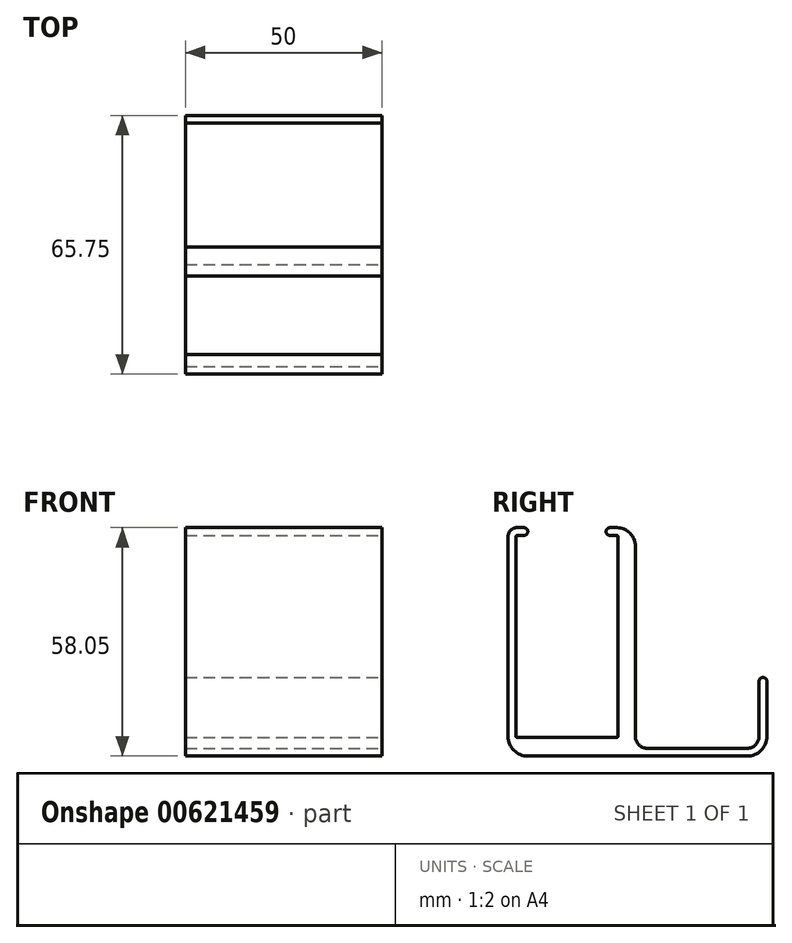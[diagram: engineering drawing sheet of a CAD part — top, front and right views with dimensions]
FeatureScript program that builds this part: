
annotation { "Feature Type Name" : "Feature", "Feature Type Description" : "" }
export const myFeature = defineFeature(function(context is Context, id is Id, definition is map)
    precondition{}
    {
        {
            var Q0;
            Q0=qCreatedBy(makeId("Right.planeOp"),FACE);
            var sketch = newSketch(context, id + "F0", { "sketchPlane" : qUnion([Q0])});
            skLineSegment(sketch, "E0.bottom", {"start": v(-33.1, 50.8) * mm, "end": v(-7.7, 50.8) * mm});
            skLineSegment(sketch, "E0.top", {"start": v(-33.1, 0) * mm, "end": v(-7.7, 0) * mm});
            skLineSegment(sketch, "E0.left", {"start": v(-33.1, 50.8) * mm, "end": v(-33.1, 0) * mm});
            skLineSegment(sketch, "E0.right", {"start": v(-7.7, 50.8) * mm, "end": v(-7.7, 0) * mm});
            skLineSegment(sketch, "E1.bottom", {"start": v(0, 0) * mm, "end": v(25.4, 0) * mm});
            skLineSegment(sketch, "E1.top", {"start": v(0, 50.8) * mm, "end": v(25.4, 50.8) * mm});
            skLineSegment(sketch, "E1.left", {"start": v(0, 0) * mm, "end": v(0, 50.8) * mm});
            skLineSegment(sketch, "E1.right", {"start": v(25.4, 0) * mm, "end": v(25.4, 50.8) * mm});
            skLineSegment(sketch, "E2", {"start": v(-33.35, -0.25) * mm, "end": v(-7.45, -0.25) * mm});
            skLineSegment(sketch, "E3", {"start": v(-7.45, -0.25) * mm, "end": v(-7.45, 51.05) * mm});
            skLineSegment(sketch, "E4", {"start": v(-7.45, 51.05) * mm, "end": v(-10.45, 51.05) * mm});
            skLineSegment(sketch, "E5", {"start": v(-33.35, -0.25) * mm, "end": v(-33.35, 51.05) * mm});
            skLineSegment(sketch, "E6", {"start": v(-33.35, 51.05) * mm, "end": v(-30.35, 51.05) * mm});
            skLineSegment(sketch, "E7", {"start": v(28.4, -3) * mm, "end": v(28.4, 15) * mm});
            skLineSegment(sketch, "E8", {"start": v(28.4, -3) * mm, "end": v(-3, -3) * mm});
            skLineSegment(sketch, "E9", {"start": v(-3, -3) * mm, "end": v(-3, 53.05) * mm});
            skLineSegment(sketch, "E10", {"start": v(-10.45, 51.05) * mm, "end": v(-10.45, 53.05) * mm});
            skLineSegment(sketch, "E11", {"start": v(-10.45, 53.05) * mm, "end": v(-3, 53.05) * mm});
            skLineSegment(sketch, "E12", {"start": v(-30.35, 53.05) * mm, "end": v(-35.35, 53.05) * mm});
            skLineSegment(sketch, "E13", {"start": v(-30.35, 51.05) * mm, "end": v(-30.35, 53.05) * mm});
            skLineSegment(sketch, "E14", {"start": v(28.4, 15) * mm, "end": v(30.4, 15) * mm});
            skLineSegment(sketch, "E15", {"start": v(30.4, 15) * mm, "end": v(30.4, -5) * mm});
            skLineSegment(sketch, "E16", {"start": v(30.4, -5) * mm, "end": v(-35.35, -5) * mm});
            skLineSegment(sketch, "E17", {"start": v(-35.35, -5) * mm, "end": v(-35.35, 53.05) * mm});
            skArc(sketch, "E18", {"start": v(-33.1, 51.05) * mm, "mid": v(-33.28, 50.98) * mm, "end": v(-33.35, 50.8) * mm});
            skArc(sketch, "E19", {"start": v(-33.1, 53.05) * mm, "mid": v(-34.7, 52.4) * mm, "end": v(-35.35, 50.8) * mm});
            skArc(sketch, "E20", {"start": v(-31.35, 51.05) * mm, "mid": v(-30.35, 52.05) * mm, "end": v(-31.35, 53.05) * mm});
            skArc(sketch, "E21", {"start": v(-9.45, 53.05) * mm, "mid": v(-10.45, 52.05) * mm, "end": v(-9.45, 51.05) * mm});
            skArc(sketch, "E22", {"start": v(-7.45, 50.8) * mm, "mid": v(-7.52, 50.98) * mm, "end": v(-7.7, 51.05) * mm});
            skArc(sketch, "E23", {"start": v(-3, 48.35) * mm, "mid": v(-4.38, 51.67) * mm, "end": v(-7.7, 53.05) * mm});
            skArc(sketch, "E24", {"start": v(-33.35, 0) * mm, "mid": v(-33.28, -0.18) * mm, "end": v(-33.1, -0.25) * mm});
            skArc(sketch, "E25", {"start": v(-7.7, -0.25) * mm, "mid": v(-7.52, -0.18) * mm, "end": v(-7.45, 0) * mm});
            skArc(sketch, "E26", {"start": v(-3, 0) * mm, "mid": v(-2.12, -2.12) * mm, "end": v(0, -3) * mm});
            skArc(sketch, "E27", {"start": v(25.4, -3) * mm, "mid": v(27.52, -2.12) * mm, "end": v(28.4, 0) * mm});
            skArc(sketch, "E28", {"start": v(30.4, 14) * mm, "mid": v(29.4, 15) * mm, "end": v(28.4, 14) * mm});
            skArc(sketch, "E29", {"start": v(25.4, -5) * mm, "mid": v(28.94, -3.54) * mm, "end": v(30.4, 0) * mm});
            skArc(sketch, "E30", {"start": v(-35.35, 0) * mm, "mid": v(-33.89, -3.54) * mm, "end": v(-30.35, -5) * mm});
            skSolve(sketch);
        }
        {
            var Q0;
            Q0=makeQuery(id+"F0.imprint","IMPRINT",FACE,{"disambiguationData":[TD([[makeQuery(id+"F0.imprint","IMPRINT",EDGE,{"derivedFrom":sQuery(id+"F0.wireOp",EDGE,"E2")}),-1.0]])]});
            var Q1;
            {var subQ3=sQuery(id+"F0.wireOp",EDGE,"E18");Q1=makeQuery(id+"F0.imprint","IMPRINT",FACE,{"disambiguationData":[TD([[makeQuery(id+"F0.imprint","IMPRINT",EDGE,{"derivedFrom":subQ3}),-1.0]])]});}
            var Q2;
            {var subQ3=sQuery(id+"F0.wireOp",EDGE,"E22");Q2=makeQuery(id+"F0.imprint","IMPRINT",FACE,{"disambiguationData":[TD([[makeQuery(id+"F0.imprint","IMPRINT",EDGE,{"derivedFrom":subQ3}),-1.0]])]});}
            var Q3;
            {var subQ3=sQuery(id+"F0.wireOp",EDGE,"E26");Q3=makeQuery(id+"F0.imprint","IMPRINT",FACE,{"disambiguationData":[TD([[makeQuery(id+"F0.imprint","IMPRINT",EDGE,{"derivedFrom":subQ3}),-1.0]])]});}
            var Q4;
            {var subQ3=sQuery(id+"F0.wireOp",EDGE,"E25");Q4=makeQuery(id+"F0.imprint","IMPRINT",FACE,{"disambiguationData":[TD([[makeQuery(id+"F0.imprint","IMPRINT",EDGE,{"derivedFrom":subQ3}),-1.0]])]});}
            var Q5;
            {var subQ3=sQuery(id+"F0.wireOp",EDGE,"E24");Q5=makeQuery(id+"F0.imprint","IMPRINT",FACE,{"disambiguationData":[TD([[makeQuery(id+"F0.imprint","IMPRINT",EDGE,{"derivedFrom":subQ3}),-1.0]])]});}
            var Q6;
            {var subQ3=sQuery(id+"F0.wireOp",EDGE,"E27");Q6=makeQuery(id+"F0.imprint","IMPRINT",FACE,{"disambiguationData":[TD([[makeQuery(id+"F0.imprint","IMPRINT",EDGE,{"derivedFrom":subQ3}),-1.0]])]});}
            extrude(context, id + "F1", {"entities" : qUnion([Q0, Q1, Q2, Q3, Q4, Q5, Q6]), "oppositeDirection" : true, "depth" : 50 * mm, "offsetDistance" : 25 * mm});
        }
    });
